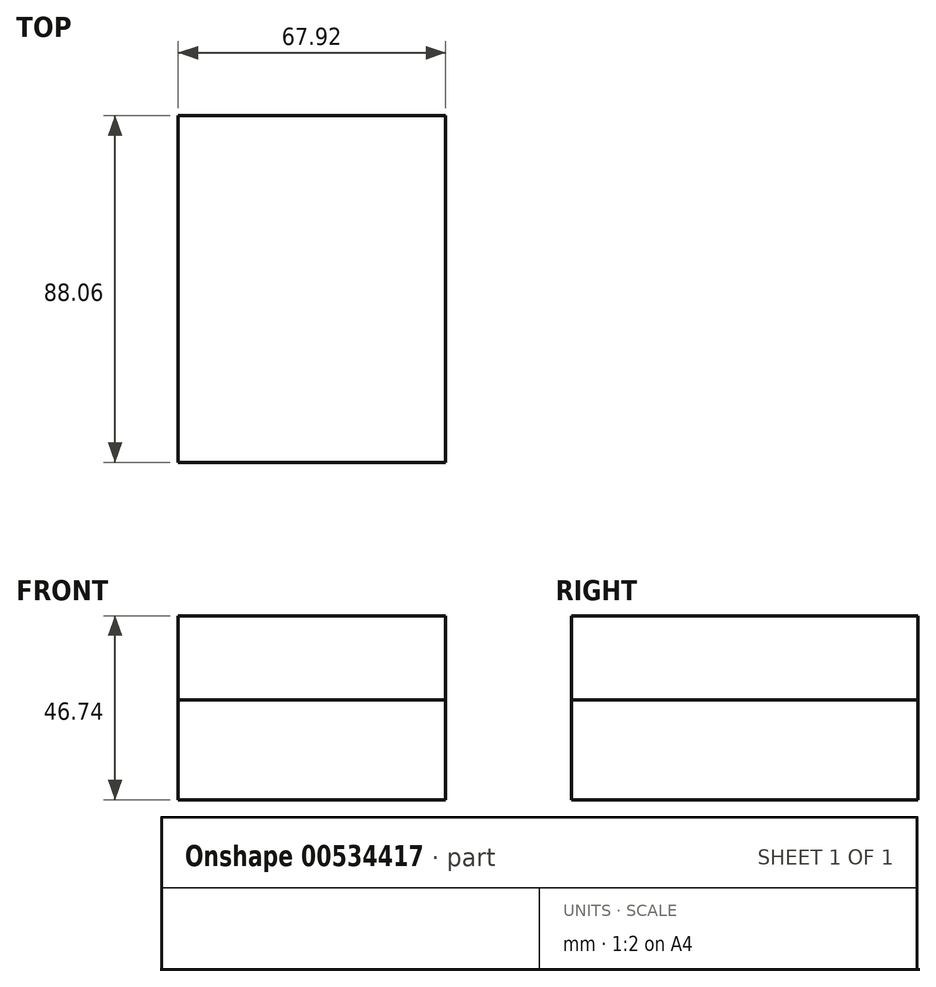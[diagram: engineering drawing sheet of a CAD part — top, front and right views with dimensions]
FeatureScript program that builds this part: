
annotation { "Feature Type Name" : "Feature", "Feature Type Description" : "" }
export const myFeature = defineFeature(function(context is Context, id is Id, definition is map)
    precondition{}
    {
        {
            var Q0;
            Q0=qCreatedBy(makeId("Top.planeOp"),FACE);
            var sketch = newSketch(context, id + "F0", { "sketchPlane" : qUnion([Q0])});
            skLineSegment(sketch, "E0.bottom", {"start": v(33.96, 44.03) * mm, "end": v(-33.96, 44.03) * mm});
            skLineSegment(sketch, "E0.top", {"start": v(33.96, -44.03) * mm, "end": v(-33.96, -44.03) * mm});
            skLineSegment(sketch, "E0.left", {"start": v(33.96, 44.03) * mm, "end": v(33.96, -44.03) * mm});
            skLineSegment(sketch, "E0.right", {"start": v(-33.96, 44.03) * mm, "end": v(-33.96, -44.03) * mm});
            skPoint(sketch, "E0.middle", {"position": v(0, 0) * mm});
            skSolve(sketch);
        }
        {
            var Q0;
            Q0 = qSketchRegion(id + "F0", true);
            extrude(context, id + "F1", {"entities" : qUnion([Q0]), "depth" : 46.74 * mm, "offsetDistance" : 25.4 * mm});
        }
        {
            var Q0;
            Q0=makeQuery(id+"F0.imprint","IMPRINT",FACE,{"disambiguationData":[TD([[makeQuery(id+"F0.imprint","IMPRINT",EDGE,{"derivedFrom":sQuery(id+"F0.wireOp",EDGE,"E0.bottom")}),1.0]])]});
            extrude(context, id + "F2", {"entities" : qUnion([Q0]), "depth" : 25.4 * mm});
        }
    });
